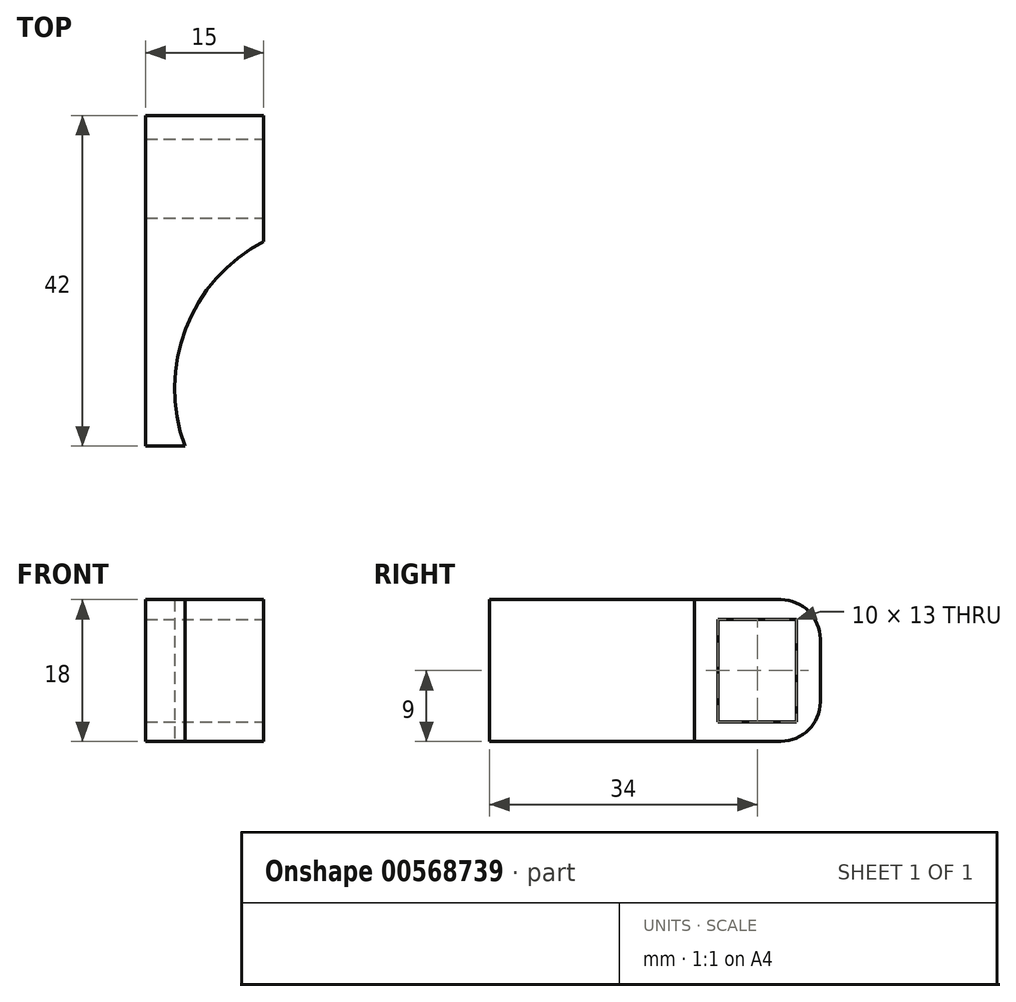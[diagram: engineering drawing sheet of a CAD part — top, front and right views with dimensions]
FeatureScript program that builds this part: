
annotation { "Feature Type Name" : "Feature", "Feature Type Description" : "" }
export const myFeature = defineFeature(function(context is Context, id is Id, definition is map)
    precondition{}
    {
        {
            var Q0;
            Q0=qCreatedBy(makeId("Top.planeOp"),FACE);
            var sketch = newSketch(context, id + "F0", { "sketchPlane" : qUnion([Q0])});
            skLineSegment(sketch, "E0", {"start": v(0, 0) * mm, "end": v(0, 30) * mm});
            skLineSegment(sketch, "E1", {"start": v(0, 30) * mm, "end": v(15, 30) * mm});
            skLineSegment(sketch, "E2", {"start": v(0, 0) * mm, "end": v(5, 0) * mm});
            skLineSegment(sketch, "E3", {"start": v(15, 30) * mm, "end": v(15, 26) * mm});
            skArc(sketch, "E4", {"start": v(15, 26) * mm, "mid": v(5.07, 14.9) * mm, "end": v(5, 0) * mm});
            skLineSegment(sketch, "E5", {"start": v(0, 30) * mm, "end": v(0, 42) * mm});
            skLineSegment(sketch, "E6", {"start": v(0, 42) * mm, "end": v(15, 42) * mm});
            skLineSegment(sketch, "E7", {"start": v(15, 42) * mm, "end": v(15, 30) * mm});
            skSolve(sketch);
        }
        {
            var Q0;
            Q0 = qSketchRegion(id + "F0", true);
            extrude(context, id + "F1", {"entities" : qUnion([Q0]), "depth" : 18 * mm, "offsetDistance" : 25 * mm});
        }
        {
            var Q0;
            Q0=makeQuery(id+"F1.opExtrude","SWEPT_FACE",FACE,{"disambiguationData":[OSD([sQuery(id+"F0.wireOp",EDGE,"E3"),sQuery(id+"F0.wireOp",EDGE,"E7")])]});
            var sketch = newSketch(context, id + "F2", { "sketchPlane" : qUnion([Q0])});
            skLineSegment(sketch, "E8.bottom", {"start": v(29, 15.5) * mm, "end": v(39, 15.5) * mm});
            skLineSegment(sketch, "E8.top", {"start": v(29, 2.5) * mm, "end": v(39, 2.5) * mm});
            skLineSegment(sketch, "E8.left", {"start": v(29, 15.5) * mm, "end": v(29, 2.5) * mm});
            skLineSegment(sketch, "E8.right", {"start": v(39, 15.5) * mm, "end": v(39, 2.5) * mm});
            skSolve(sketch);
        }
        {
            var Q0;
            Q0 = qSketchRegion(id + "F2", true);
            extrude(context, id + "F3", {"entities" : qUnion([Q0]), "operationType" : NewBodyOperationType.REMOVE, "oppositeDirection" : true, "depth" : 25 * mm, "offsetDistance" : 25 * mm});
        }
        {
            var Q0;
            Q0=makeQuery(id+"F1.opExtrude","CAP_EDGE",EDGE,{"disambiguationData":[OSD([sQuery(id+"F0.wireOp",EDGE,"E6")])],"isStart":false});
            var Q1;
            Q1=makeQuery(id+"F1.opExtrude","CAP_EDGE",EDGE,{"disambiguationData":[OSD([sQuery(id+"F0.wireOp",EDGE,"E6")])],"isStart":true});
            fillet(context, id + "F4", {"entities" : qUnion([Q0, Q1]), "radius" : 5 * mm, "tangentPropagation" : true, "allowEdgeOverflow" : false});
        }
    });
